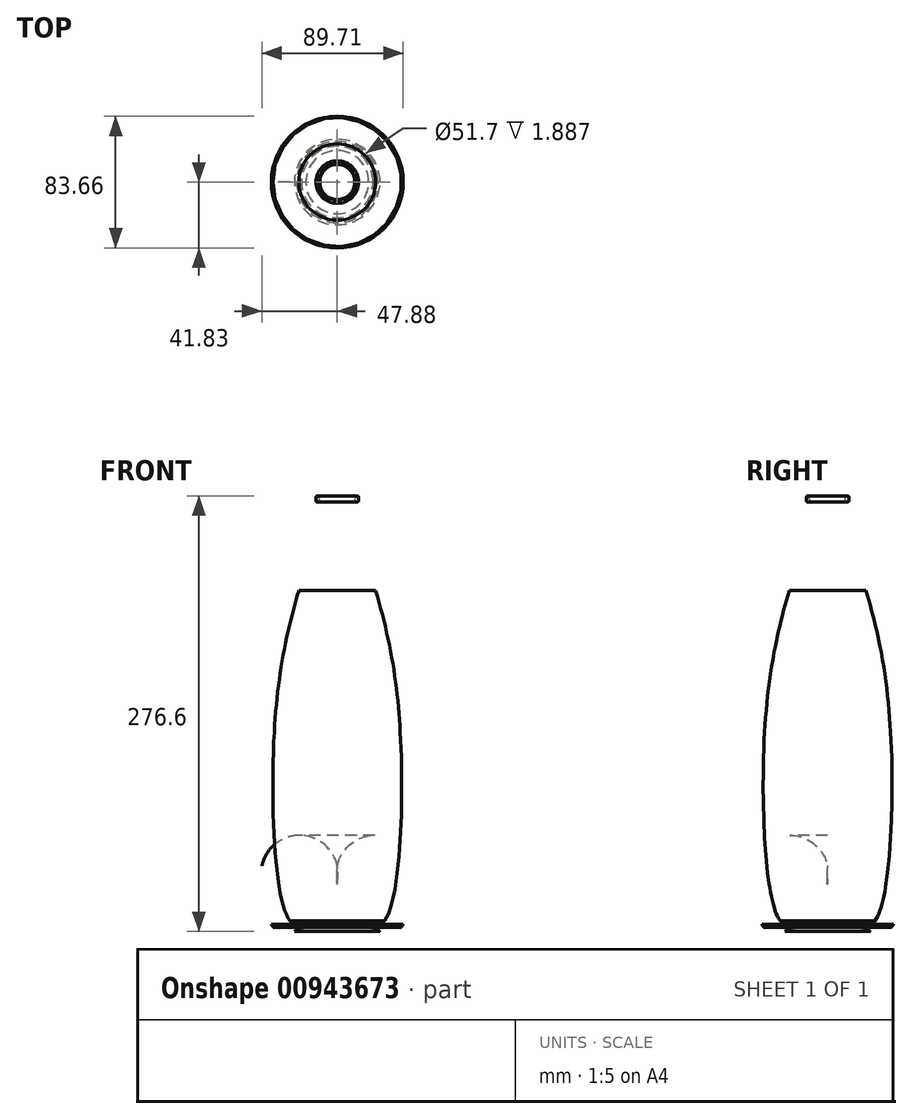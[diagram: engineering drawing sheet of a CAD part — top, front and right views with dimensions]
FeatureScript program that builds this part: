
annotation { "Feature Type Name" : "Feature", "Feature Type Description" : "" }
export const myFeature = defineFeature(function(context is Context, id is Id, definition is map)
    precondition{}
    {
        {
            var Q0;
            Q0=qCreatedBy(makeId("Front.planeOp"),FACE);
            var sketch = newSketch(context, id + "F0", { "sketchPlane" : qUnion([Q0])});
            skLineSegment(sketch, "E0", {"start": v(0, 0) * mm, "end": v(0, 270) * mm});
            skLineSegment(sketch, "E1", {"start": v(-9.5, 270) * mm, "end": v(-8.58, 259.44) * mm});
            skPoint(sketch, "E2", {"position": v(0, 246) * mm});
            skLineSegment(sketch, "E3", {"start": v(-77.67, 256) * mm, "end": v(0, 256) * mm});
            skLineSegment(sketch, "E4", {"start": v(-40, 120) * mm, "end": v(118.95, 120) * mm});
            skLineSegment(sketch, "E5", {"start": v(0, 0) * mm, "end": v(-30, 0) * mm});
            skPoint(sketch, "E6", {"position": v(0, 27) * mm});
            skLineSegment(sketch, "E7", {"start": v(-9.5, 270) * mm, "end": v(0, 270) * mm});
            skPoint(sketch, "E8", {"position": v(-20, 0) * mm});
            skFitSpline(sketch, "E9", {"points": [v(0, 27) * mm, v(-20, 0) * mm, v(-30, 0) * mm, v(-40, 120) * mm, v(-8.28, 256) * mm], "startDerivative": vector(-50.01, -221.22) * mm, "endDerivative": vector(151.7, 395.11) * mm});
            skArc(sketch, "E10.filletArc", {"start": v(-9.5, 252.8) * mm, "mid": v(-8.66, 256.07) * mm, "end": v(-8.58, 259.44) * mm});
            skLineSegment(sketch, "E11", {"start": v(0, 210) * mm, "end": v(-76.1, 210) * mm});
            skPoint(sketch, "E12", {"position": v(-24.3, 210) * mm});
            skSolve(sketch);
        }
        {
            var Q0;
            Q0=qCreatedBy(makeId("Front.planeOp"),FACE);
            var sketch = newSketch(context, id + "F1", { "sketchPlane" : qUnion([Q0])});
            skLineSegment(sketch, "E13.0.0", {"start": v(-40, 120) * mm, "end": v(-42.85, 120) * mm});
            skFitSpline(sketch, "E13.0.1", {"points": [v(-8.28, 256) * mm, v(-27.1, 206.98) * mm, v(-46.24, 138.17) * mm, v(-38.6, -6.34) * mm, v(-17.98, -0.72) * mm, v(-3.04, 13.54) * mm, v(0, 27) * mm]});
            skLineSegment(sketch, "E13.0.4", {"start": v(0, 27) * mm, "end": v(0, 120) * mm});
            skLineSegment(sketch, "E14", {"start": v(-49.37, -2.11) * mm, "end": v(37.47, -2.11) * mm});
            skPoint(sketch, "E15", {"position": v(-25.85, -2.11) * mm});
            skLineSegment(sketch, "E16", {"start": v(-25.85, -2.11) * mm, "end": v(-25.85, -31.53) * mm});
            skLineSegment(sketch, "E17", {"start": v(-45.24, -4) * mm, "end": v(-6, -4) * mm});
            skPoint(sketch, "E18", {"position": v(0, 25) * mm});
            skLineSegment(sketch, "E19.0", {"start": v(-11.5, 270) * mm, "end": v(-10.57, 259.26) * mm});
            skArc(sketch, "E20.0", {"start": v(-11.38, 253.49) * mm, "mid": v(-10.64, 256.33) * mm, "end": v(-10.57, 259.26) * mm});
            skPoint(sketch, "E21", {"position": v(-42.85, 120) * mm});
            skPoint(sketch, "E22", {"position": v(-20, -4) * mm});
            skPoint(sketch, "E23", {"position": v(-31.56, -4) * mm});
            skFitSpline(sketch, "E24", {"points": [v(0, 25) * mm, v(-20, -4) * mm, v(-31.56, -4) * mm, v(-42.85, 120) * mm, v(-11.38, 253.49) * mm], "startDerivative": vector(-33.89, -165.62) * mm, "endDerivative": vector(107.89, 254.87) * mm});
            skLineSegment(sketch, "E25.0", {"start": v(0, 210) * mm, "end": v(-76.1, 210) * mm});
            skPoint(sketch, "E26", {"position": v(-26.58, 210) * mm});
            skLineSegment(sketch, "E27.0", {"start": v(-9.45, 269.4) * mm, "end": v(-8.89, 263.03) * mm});
            skPoint(sketch, "E28.0", {"position": v(-8.28, 256) * mm});
            skArc(sketch, "E29.0", {"start": v(-9.5, 252.8) * mm, "mid": v(-8.66, 256.07) * mm, "end": v(-8.58, 259.44) * mm});
            skPoint(sketch, "E30.orphan", {"position": v(-8.58, 259.44) * mm});
            skLineSegment(sketch, "E31.0", {"start": v(-11.5, 270) * mm, "end": v(-10.1, 270) * mm});
            skPoint(sketch, "E32.orphan", {"position": v(0, 270) * mm});
            skPoint(sketch, "E33.visualSharp", {"position": v(-9.5, 270) * mm});
            skArc(sketch, "E33.filletArc", {"start": v(-9.45, 269.4) * mm, "mid": v(-9.66, 269.83) * mm, "end": v(-10.1, 270) * mm});
            skLineSegment(sketch, "E34", {"start": v(-11.5, 270) * mm, "end": v(-12.5, 270) * mm});
            skLineSegment(sketch, "E35", {"start": v(-13.5, 269) * mm, "end": v(-13.5, 267) * mm});
            skLineSegment(sketch, "E36", {"start": v(-12.5, 266) * mm, "end": v(-11.16, 266) * mm});
            skPoint(sketch, "E37.visualSharp", {"position": v(-13.5, 270) * mm});
            skArc(sketch, "E37.filletArc", {"start": v(-12.5, 270) * mm, "mid": v(-13.21, 269.7) * mm, "end": v(-13.5, 269) * mm});
            skPoint(sketch, "E38.visualSharp", {"position": v(-13.5, 266) * mm});
            skArc(sketch, "E38.filletArc", {"start": v(-13.5, 267) * mm, "mid": v(-13.21, 266.3) * mm, "end": v(-12.5, 266) * mm});
            skLineSegment(sketch, "E39", {"start": v(-8.58, 259.44) * mm, "end": v(-8.89, 263.03) * mm});
            skFitSpline(sketch, "E40.0", {"points": [v(0, 27) * mm, v(-3.04, 13.54) * mm, v(-17.98, -0.72) * mm, v(-38.6, -6.34) * mm, v(-46.24, 138.17) * mm, v(-27.1, 206.98) * mm, v(-8.28, 256) * mm]});
            skLineSegment(sketch, "E41.0", {"start": v(0, 0) * mm, "end": v(-30, 0) * mm});
            skLineSegment(sketch, "E42.0", {"start": v(0, 0) * mm, "end": v(0, 270) * mm});
            skSolve(sketch);
        }
        {
            var Q0;
            {var subQ0=sQuery(id+"F0.wireOp",EDGE,"OEpXPx8m-CtHQ-uhmr-Ckkb-ua0WuGHDi7NN");var subQ1=sQuery(id+"F0.wireOp",EDGE,"E0");var subQ2=makeQuery(id+"F0.imprint","INTERSECT",VERTEX,{"derivedFrom":[subQ1,subQ0]});Q0=makeQuery(id+"F0.imprint","IMPRINT",FACE,{"disambiguationData":[TD([[makeQuery(id+"F0.imprint","IMPRINT",EDGE,{"disambiguationData":[TD([[subQ2,1.0]])],"derivedFrom":subQ1}),1.0]])]});}
            var Q1;
            {var subQ0=sQuery(id+"F0.wireOp",EDGE,"E9");var subQ1=sQuery(id+"F0.wireOp",EDGE,"E5");var subQ2=makeQuery(id+"F0.imprint","INTERSECT",VERTEX,{"disambiguationData":[OD(0.0)],"derivedFrom":[subQ1,subQ0]});Q1=makeQuery(id+"F0.imprint","IMPRINT",FACE,{"disambiguationData":[TD([[makeQuery(id+"F0.imprint","IMPRINT",EDGE,{"disambiguationData":[TD([[subQ2,1.0]])],"derivedFrom":subQ1}),1.0]])]});}
            var Q2;
            {var subQ0=sQuery(id+"F0.wireOp",EDGE,"E9");var subQ1=sQuery(id+"F0.wireOp",EDGE,"E0");var subQ2=makeQuery(id+"F0.imprint","INTERSECT",VERTEX,{"derivedFrom":[subQ1,subQ0]});Q2=makeQuery(id+"F0.imprint","IMPRINT",FACE,{"disambiguationData":[TD([[makeQuery(id+"F0.imprint","IMPRINT",EDGE,{"disambiguationData":[TD([[subQ2,-1.0]])],"derivedFrom":subQ1}),1.0]])]});}
            var Q3;
            {var subQ0=sQuery(id+"F0.wireOp",EDGE,"E11");var subQ1=sQuery(id+"F0.wireOp",EDGE,"E0");var subQ2=makeQuery(id+"F0.imprint","INTERSECT",VERTEX,{"derivedFrom":[subQ1,subQ0]});Q3=makeQuery(id+"F0.imprint","IMPRINT",FACE,{"disambiguationData":[TD([[makeQuery(id+"F0.imprint","IMPRINT",EDGE,{"disambiguationData":[TD([[subQ2,1.0]])],"derivedFrom":subQ1}),1.0]])]});}
            var Q4;
            Q4=sQuery(id+"F0.wireOp",EDGE,"E0");
            revolve(context, id + "F2", {"surfaceOperationType" : NewSurfaceOperationType.NEW, "entities" : qUnion([Q0, Q1, Q2, Q3]), "axis" : qUnion([Q4]), "revolveType" : RevolveType.FULL});
        }
        {
            var Q0;
            {var subQ0=sQuery(id+"F1.wireOp",EDGE,"E42.0");var subQ1=sQuery(id+"F1.wireOp",EDGE,"E24");var subQ2=makeQuery(id+"F1.imprint","INTERSECT",VERTEX,{"derivedFrom":[subQ1,subQ0]});Q0=makeQuery(id+"F1.imprint","IMPRINT",FACE,{"disambiguationData":[TD([[makeQuery(id+"F1.imprint","IMPRINT",EDGE,{"disambiguationData":[TD([[subQ2,-1.0]])],"derivedFrom":subQ1}),-1.0]])]});}
            var Q1;
            {var subQ1=sQuery(id+"F1.wireOp",EDGE,"E14");var subQ3=sQuery(id+"F1.wireOp",EDGE,"E24");var subQ4=makeQuery(id+"F1.imprint","INTERSECT",VERTEX,{"disambiguationData":[OD(1.0)],"derivedFrom":[subQ1,subQ3]});Q1=makeQuery(id+"F1.imprint","IMPRINT",FACE,{"disambiguationData":[TD([[makeQuery(id+"F1.imprint","IMPRINT",EDGE,{"disambiguationData":[TD([[subQ4,1.0]])],"derivedFrom":subQ3}),-1.0]])]});}
            var Q2;
            {var subQ3=sQuery(id+"F1.wireOp",EDGE,"E24");var subQ5=sQuery(id+"F1.wireOp",EDGE,"E17");var subQ6=makeQuery(id+"F1.imprint","INTERSECT",VERTEX,{"disambiguationData":[OD(1.0)],"derivedFrom":[subQ5,subQ3]});Q2=makeQuery(id+"F1.imprint","IMPRINT",FACE,{"disambiguationData":[TD([[makeQuery(id+"F1.imprint","IMPRINT",EDGE,{"disambiguationData":[TD([[subQ6,1.0]])],"derivedFrom":subQ5}),1.0]])]});}
            var Q3;
            {var subQ0=sQuery(id+"F1.wireOp",EDGE,"E24");var subQ1=sQuery(id+"F1.wireOp",EDGE,"E16");var subQ2=makeQuery(id+"F1.imprint","INTERSECT",VERTEX,{"derivedFrom":[subQ1,subQ0]});Q3=makeQuery(id+"F1.imprint","IMPRINT",FACE,{"disambiguationData":[TD([[makeQuery(id+"F1.imprint","IMPRINT",EDGE,{"disambiguationData":[TD([[subQ2,1.0]])],"derivedFrom":subQ1}),1.0]])]});}
            var Q4;
            {var subQ0=sQuery(id+"F1.wireOp",EDGE,"E24");var subQ1=sQuery(id+"F1.wireOp",EDGE,"E16");var subQ2=makeQuery(id+"F1.imprint","INTERSECT",VERTEX,{"derivedFrom":[subQ1,subQ0]});Q4=makeQuery(id+"F1.imprint","IMPRINT",FACE,{"disambiguationData":[TD([[makeQuery(id+"F1.imprint","IMPRINT",EDGE,{"disambiguationData":[TD([[subQ2,1.0]])],"derivedFrom":subQ1}),-1.0]])]});}
            var Q5;
            {var subQ3=sQuery(id+"F1.wireOp",EDGE,"E24");var subQ5=sQuery(id+"F1.wireOp",EDGE,"E17");var subQ7=makeQuery(id+"F1.imprint","INTERSECT",VERTEX,{"disambiguationData":[OD(0.0)],"derivedFrom":[subQ5,subQ3]});Q5=makeQuery(id+"F1.imprint","IMPRINT",FACE,{"disambiguationData":[TD([[makeQuery(id+"F1.imprint","IMPRINT",EDGE,{"disambiguationData":[TD([[subQ7,-1.0]])],"derivedFrom":subQ5}),1.0]])]});}
            var Q6;
            {var subQ4=sQuery(id+"F1.wireOp",EDGE,"E13.0.0");Q6=makeQuery(id+"F1.imprint","IMPRINT",FACE,{"disambiguationData":[TD([[makeQuery(id+"F1.imprint","IMPRINT",EDGE,{"derivedFrom":subQ4}),1.0]])]});}
            var Q7;
            {var subQ0=sQuery(id+"F1.wireOp",EDGE,"E13.0.0");Q7=makeQuery(id+"F1.imprint","IMPRINT",FACE,{"disambiguationData":[TD([[makeQuery(id+"F1.imprint","IMPRINT",EDGE,{"derivedFrom":subQ0}),-1.0]])]});}
            var Q8;
            {var subQ4=sQuery(id+"F1.wireOp",EDGE,"E20.0");Q8=makeQuery(id+"F1.imprint","IMPRINT",FACE,{"disambiguationData":[TD([[makeQuery(id+"F1.imprint","IMPRINT",EDGE,{"derivedFrom":subQ4}),-1.0]])]});}
            var Q9;
            {var subQ0=sQuery(id+"F1.wireOp",EDGE,"E34");Q9=makeQuery(id+"F1.imprint","IMPRINT",FACE,{"disambiguationData":[TD([[makeQuery(id+"F1.imprint","IMPRINT",EDGE,{"derivedFrom":subQ0}),1.0]])]});}
            var Q10;
            Q10=sQuery(id+"F1.wireOp",EDGE,"E42.0");
            revolve(context, id + "F3", {"surfaceOperationType" : NewSurfaceOperationType.NEW, "entities" : qUnion([Q0, Q1, Q2, Q3, Q4, Q5, Q6, Q7, Q8, Q9]), "axis" : qUnion([Q10]), "revolveType" : RevolveType.FULL});
        }
    });
